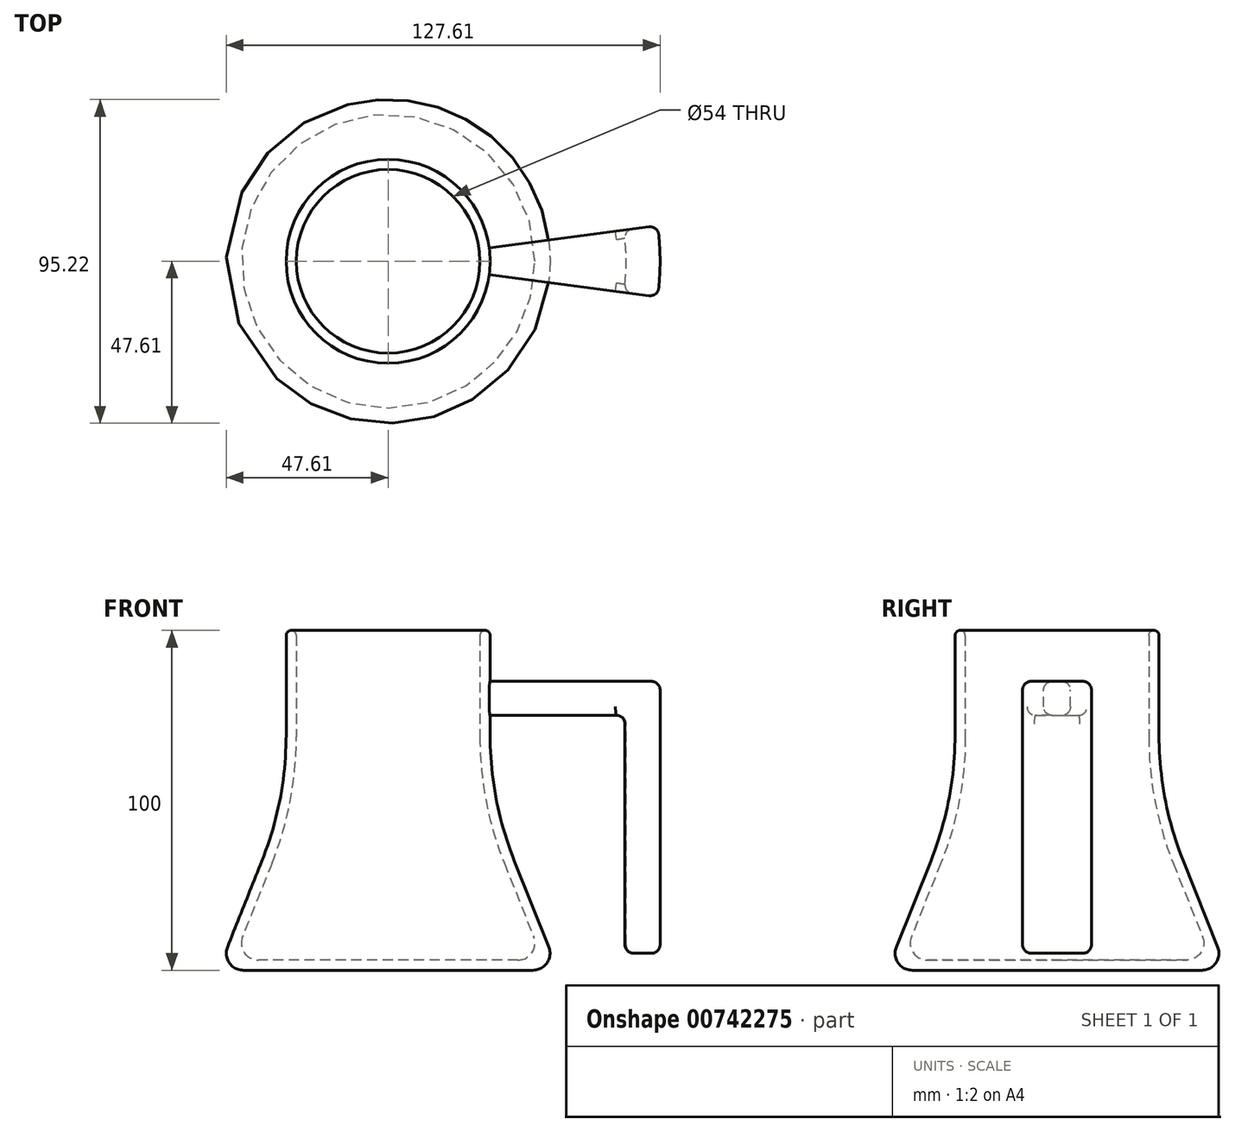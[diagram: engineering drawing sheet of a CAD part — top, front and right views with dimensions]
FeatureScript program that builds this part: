
annotation { "Feature Type Name" : "Feature", "Feature Type Description" : "" }
export const myFeature = defineFeature(function(context is Context, id is Id, definition is map)
    precondition{}
    {
        {
            var Q0;
            Q0=qCreatedBy(makeId("Top.planeOp"),FACE);
            var sketch = newSketch(context, id + "F0", { "sketchPlane" : qUnion([Q0])});
            skCircle(sketch, "E0", {"center": v(0, 0) * mm, "radius": 50 * mm});
            skSolve(sketch);
        }
        {
            var Q0;
            Q0=makeQuery(id+"F0.imprint","IMPRINT",FACE,{"disambiguationData":[TD([[makeQuery(id+"F0.imprint","IMPRINT",EDGE,{"derivedFrom":sQuery(id+"F0.wireOp",EDGE,"E0")}),1.0]])]});
            cPlane(context, id + "F1", {"entities" : qUnion([Q0]), "cplaneType" : CPlaneType.OFFSET, "offset" : 50 * mm, "width" : 150 * mm, "height" : 150 * mm});
        }
        {
            var Q0;
            Q0=qCreatedBy(id+"F1.planeOp",FACE);
            var sketch = newSketch(context, id + "F2", { "sketchPlane" : qUnion([Q0])});
            skCircle(sketch, "E1", {"center": v(0, 0) * mm, "radius": 30 * mm});
            skSolve(sketch);
        }
        {
            var Q0;
            Q0=makeQuery(id+"F0.imprint","IMPRINT",FACE,{"disambiguationData":[TD([[makeQuery(id+"F0.imprint","IMPRINT",EDGE,{"derivedFrom":sQuery(id+"F0.wireOp",EDGE,"E0")}),1.0]])]});
            var Q1;
            Q1=makeQuery(id+"F2.imprint","IMPRINT",FACE,{"disambiguationData":[TD([[makeQuery(id+"F2.imprint","IMPRINT",EDGE,{"derivedFrom":sQuery(id+"F2.wireOp",EDGE,"E1")}),1.0]])]});
            loft(context, id + "F3", {"sheetProfilesArray" : [{ "sheetProfileEntities" : qUnion([Q0]) }, { "sheetProfileEntities" : qUnion([Q1]) }]});
        }
        {
            var Q0;
            Q0=makeQuery(id+"F3.opLoft","CAP_FACE",FACE,{"disambiguationData":[OSD([makeQuery(id+"F2.imprint","IMPRINT",FACE,{"disambiguationData":[TD([[makeQuery(id+"F2.imprint","IMPRINT",EDGE,{"derivedFrom":sQuery(id+"F2.wireOp",EDGE,"E1")}),1.0]])]})])],"isStart":true});
            extrude(context, id + "F4", {"entities" : qUnion([Q0]), "operationType" : NewBodyOperationType.ADD, "depth" : 50 * mm, "offsetDistance" : 25 * mm});
        }
        {
            var Q0;
            Q0=makeQuery(id+"F4.opExtrude","CAP_FACE",FACE,{"disambiguationData":[OSD([makeQuery(id+"F2.imprint","IMPRINT",FACE,{"disambiguationData":[TD([[makeQuery(id+"F2.imprint","IMPRINT",EDGE,{"derivedFrom":sQuery(id+"F2.wireOp",EDGE,"E1")}),1.0]])]})])],"isStart":false});
            shell(context, id + "F5", {"entities" : qUnion([Q0]), "thickness" : 3 * mm});
        }
        {
            var Q0;
            Q0=makeQuery(id+"F4.opExtrude","CAP_EDGE",EDGE,{"disambiguationData":[OSD([sQuery(id+"F2.wireOp",EDGE,"E1")])],"isStart":false});
            var Q1;
            {var subQ0=sQuery(id+"F2.wireOp",EDGE,"E1");Q1=makeQuery(id+"F5.opShell","OFFSET_EDGE",EDGE,{"disambiguationData":[OSD([subQ0]),TDD([makeQuery(id+"F4.opExtrude","CAP_EDGE",EDGE,{"disambiguationData":[OSD([subQ0])],"isStart":false})])]});}
            fillet(context, id + "F6", {"entities" : qUnion([Q0, Q1]), "radius" : 1.5 * mm, "tangentPropagation" : true, "allowEdgeOverflow" : false});
        }
        {
            var Q0;
            Q0=makeQuery(id+"F3.opLoft","CAP_FACE",FACE,{"disambiguationData":[OSD([makeQuery(id+"F0.imprint","IMPRINT",FACE,{"disambiguationData":[TD([[makeQuery(id+"F0.imprint","IMPRINT",EDGE,{"derivedFrom":sQuery(id+"F0.wireOp",EDGE,"E0")}),1.0]])]})])],"isStart":true});
            var Q1;
            Q1=makeQuery(id+"F5.opShell","OFFSET_EDGE",EDGE,{"disambiguationData":[OSD([sQuery(id+"F0.wireOp",EDGE,"E0")])]});
            fillet(context, id + "F7", {"entities" : qUnion([Q0, Q1]), "radius" : 5 * mm, "tangentPropagation" : true, "allowEdgeOverflow" : false});
        }
        {
            var Q0;
            Q0=qCreatedBy(makeId("Front.planeOp"),FACE);
            var sketch = newSketch(context, id + "F8", { "sketchPlane" : qUnion([Q0])});
            skLineSegment(sketch, "E2", {"start": v(0, 80) * mm, "end": v(0, 0) * mm, "construction": true});
            skLineSegment(sketch, "E3", {"start": v(0, 80) * mm, "end": v(30, 80) * mm, "construction": true});
            skLineSegment(sketch, "E4", {"start": v(30, 80) * mm, "end": v(30, 85) * mm});
            skLineSegment(sketch, "E5", {"start": v(30, 80) * mm, "end": v(30, 75) * mm});
            skLineSegment(sketch, "E6", {"start": v(30, 85) * mm, "end": v(80, 85) * mm});
            skLineSegment(sketch, "E7", {"start": v(80, 85) * mm, "end": v(80, 5) * mm});
            skLineSegment(sketch, "E8", {"start": v(30, 75) * mm, "end": v(70, 75) * mm});
            skLineSegment(sketch, "E9", {"start": v(70, 75) * mm, "end": v(70, 5) * mm});
            skLineSegment(sketch, "E10", {"start": v(70, 5) * mm, "end": v(80, 5) * mm});
            skSolve(sketch);
        }
        {
            var Q0;
            Q0=qSketchRegion(id+"F8",true);
            var Q1;
            Q1=sQuery(id+"F8.wireOp",EDGE,"E2");
            revolve(context, id + "F9", {"operationType" : NewBodyOperationType.ADD, "surfaceOperationType" : NewSurfaceOperationType.NEW, "entities" : qUnion([Q0]), "axis" : qUnion([Q1]), "revolveType" : RevolveType.SYMMETRIC, "angle" : 15 * degree});
        }
        {
            var Q0;
            Q0=makeQuery(id+"F9.opRevolve","CAP_EDGE",EDGE,{"disambiguationData":[OSD([sQuery(id+"F8.wireOp",EDGE,"E6")])],"isStart":false});
            var Q1;
            Q1=makeQuery(id+"F9.opRevolve","CAP_EDGE",EDGE,{"disambiguationData":[OSD([sQuery(id+"F8.wireOp",EDGE,"E6")])],"isStart":true});
            var Q2;
            Q2=makeQuery(id+"F9.opRevolve","CAP_EDGE",EDGE,{"disambiguationData":[OSD([sQuery(id+"F8.wireOp",EDGE,"E7")])],"isStart":true});
            var Q3;
            Q3=makeQuery(id+"F9.opRevolve","CAP_EDGE",EDGE,{"disambiguationData":[OSD([sQuery(id+"F8.wireOp",EDGE,"E7")])],"isStart":false});
            var Q4;
            Q4=makeQuery(id+"F9.opRevolve","SWEPT_EDGE",EDGE,{"disambiguationData":[OSD([sQuery(id+"F8.wireOp",EDGE,"E6"),sQuery(id+"F8.wireOp",EDGE,"E7")])]});
            var Q5;
            Q5=makeQuery(id+"F9.opRevolve","SWEPT_EDGE",EDGE,{"disambiguationData":[OSD([sQuery(id+"F8.wireOp",EDGE,"E7"),sQuery(id+"F8.wireOp",EDGE,"E10")])]});
            var Q6;
            Q6=makeQuery(id+"F9.opRevolve","CAP_EDGE",EDGE,{"disambiguationData":[OSD([sQuery(id+"F8.wireOp",EDGE,"E10")])],"isStart":true});
            var Q7;
            Q7=makeQuery(id+"F9.opRevolve","CAP_EDGE",EDGE,{"disambiguationData":[OSD([sQuery(id+"F8.wireOp",EDGE,"E10")])],"isStart":false});
            var Q8;
            Q8=makeQuery(id+"F9.opRevolve","CAP_EDGE",EDGE,{"disambiguationData":[OSD([sQuery(id+"F8.wireOp",EDGE,"E9")])],"isStart":true});
            var Q9;
            Q9=makeQuery(id+"F9.opRevolve","CAP_EDGE",EDGE,{"disambiguationData":[OSD([sQuery(id+"F8.wireOp",EDGE,"E9")])],"isStart":false});
            var Q10;
            Q10=makeQuery(id+"F9.opRevolve","CAP_EDGE",EDGE,{"disambiguationData":[OSD([sQuery(id+"F8.wireOp",EDGE,"E8")])],"isStart":true});
            var Q11;
            Q11=makeQuery(id+"F9.opRevolve","CAP_EDGE",EDGE,{"disambiguationData":[OSD([sQuery(id+"F8.wireOp",EDGE,"E8")])],"isStart":false});
            var Q12;
            Q12=makeQuery(id+"F9.opRevolve","SWEPT_EDGE",EDGE,{"disambiguationData":[OSD([sQuery(id+"F8.wireOp",EDGE,"E9"),sQuery(id+"F8.wireOp",EDGE,"E10")])]});
            var Q13;
            Q13=makeQuery(id+"F9.opRevolve","SWEPT_EDGE",EDGE,{"disambiguationData":[OSD([sQuery(id+"F8.wireOp",EDGE,"E8"),sQuery(id+"F8.wireOp",EDGE,"E9")])]});
            fillet(context, id + "F10", {"entities" : qUnion([Q0, Q1, Q2, Q3, Q4, Q5, Q6, Q7, Q8, Q9, Q10, Q11, Q12, Q13]), "radius" : 2.5 * mm, "tangentPropagation" : true, "allowEdgeOverflow" : false});
        }
        {
            var Q0;
            {var subQ0=sQuery(id+"F2.wireOp",EDGE,"E1");Q0=makeQuery(id+"F4.boolean.opBoolean","MERGE",EDGE,{"derivedFrom":[makeQuery(id+"F3.opLoft","MID_CAP_EDGE",EDGE,{"disambiguationData":[OSD([subQ0])],"capPos":1.0}),makeQuery(id+"F4.opExtrude","CAP_EDGE",EDGE,{"disambiguationData":[OSD([subQ0])],"isStart":true})]});}
            var Q1;
            {var subQ0=sQuery(id+"F2.wireOp",EDGE,"E1");Q1=makeQuery(id+"F5.opShell","OFFSET_EDGE",EDGE,{"disambiguationData":[OSD([subQ0]),TDD([makeQuery(id+"F4.boolean.opBoolean","MERGE",EDGE,{"derivedFrom":[makeQuery(id+"F3.opLoft","MID_CAP_EDGE",EDGE,{"disambiguationData":[OSD([subQ0])],"capPos":1.0}),makeQuery(id+"F4.opExtrude","CAP_EDGE",EDGE,{"disambiguationData":[OSD([subQ0])],"isStart":true})]})])]});}
            fillet(context, id + "F11", {"entities" : qUnion([Q0, Q1]), "radius" : 100 * mm, "tangentPropagation" : true, "allowEdgeOverflow" : false});
        }
    });
